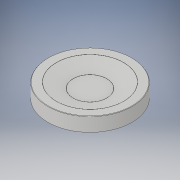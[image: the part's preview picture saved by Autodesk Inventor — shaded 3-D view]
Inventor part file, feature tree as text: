
AUTODESK INVENTOR PART (.ipt)
format: ipt  version: 2019.4 (Build 234330000, 330)  size: 129,024 bytes
history: native  units: mm
features: fillet x3, other x1, revolve x1, sketch x1
ambient origin geometry x8: Origin, YZ Plane, XZ Plane, XY Plane, X Axis, Y Axis, Z Axis, Center Point
bodies: Body1 (feature_tree)
feature tree (6):
  other  "Sólido1"
  revolve  "Revolución1"  [1 undecoded]
  fillet  "Empalme1"  Radius=300.0mm
  fillet  "Empalme2"  Radius=1200.0mm
  fillet  "Empalme3"  Radius=300.0mm
  sketch  "Boceto1"  dims[d0=1000.0mm d1=3000.0mm d2=300.0mm d4=1200.0mm d5=300.0mm d6=90.0deg d7=30.0mm d8=30.0mm d9=30.0mm]
note: 1 required parameter value undecoded (feature->parameter linkage not recoverable at this tier; creation-order binding heuristic only, values carry confidence <= 0.55)
